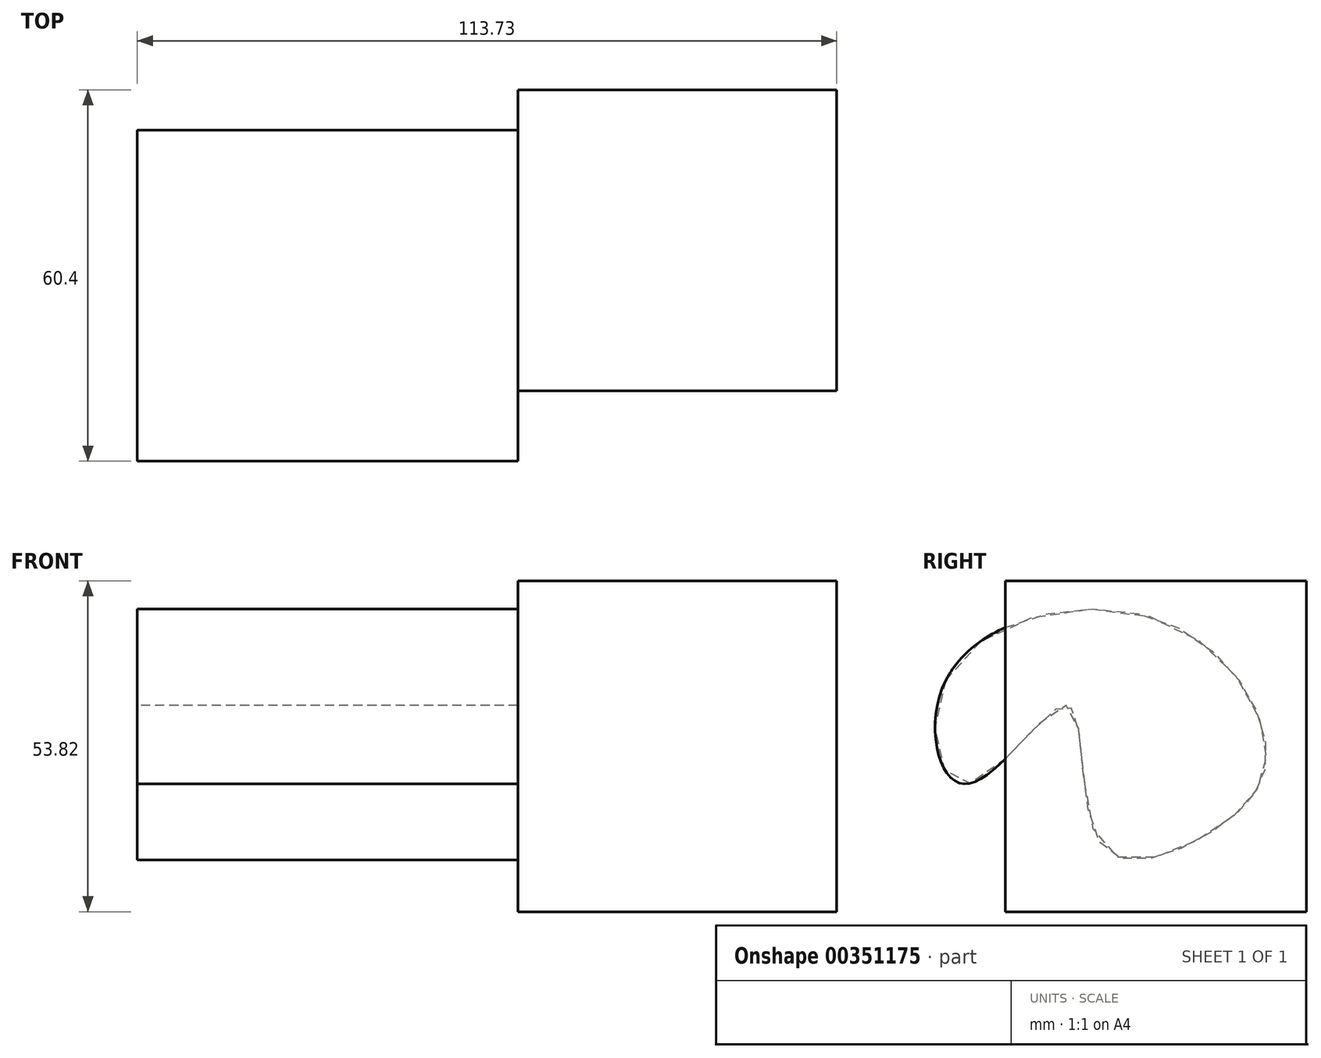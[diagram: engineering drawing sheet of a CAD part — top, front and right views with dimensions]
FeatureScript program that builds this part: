
annotation { "Feature Type Name" : "Feature", "Feature Type Description" : "" }
export const myFeature = defineFeature(function(context is Context, id is Id, definition is map)
    precondition{}
    {
        {
            var Q0;
            Q0=qCreatedBy(makeId("Top.planeOp"),FACE);
            var sketch = newSketch(context, id + "F0", { "sketchPlane" : qUnion([Q0])});
            skLineSegment(sketch, "E0.bottom", {"start": v(-24.41, 23.75) * mm, "end": v(27.4, 23.75) * mm});
            skLineSegment(sketch, "E0.top", {"start": v(-24.41, -25.2) * mm, "end": v(27.4, -25.2) * mm});
            skLineSegment(sketch, "E0.left", {"start": v(-24.41, 23.75) * mm, "end": v(-24.41, -25.2) * mm});
            skLineSegment(sketch, "E0.right", {"start": v(27.4, 23.75) * mm, "end": v(27.4, -25.2) * mm});
            skSolve(sketch);
        }
        {
            var Q0;
            Q0=makeQuery(id+"F0.imprint","IMPRINT",FACE,{"disambiguationData":[TD([[makeQuery(id+"F0.imprint","IMPRINT",EDGE,{"derivedFrom":sQuery(id+"F0.wireOp",EDGE,"E0.bottom")}),-1.0]])]});
            extrude(context, id + "F1", {"entities" : qUnion([Q0]), "depth" : 53.82 * mm});
        }
        {
            var Q0;
            Q0=makeQuery(id+"F1.opExtrude","SWEPT_FACE",FACE,{"disambiguationData":[OSD([sQuery(id+"F0.wireOp",EDGE,"E0.left")])]});
            var sketch = newSketch(context, id + "F2", { "sketchPlane" : qUnion([Q0])});
            skFitSpline(sketch, "E1", {"points": [v(34.9, 37.67) * mm, v(0, 47.45) * mm, v(-17.21, 26.05) * mm, v(-8.64, 13.2) * mm, v(9.6, 10.85) * mm, v(15.15, 33.53) * mm, v(31.5, 20.79) * mm, v(34.9, 37.67) * mm]});
            skSolve(sketch);
        }
        {
            var Q0;
            {var subQ0=sQuery(id+"F2.wireOp",EDGE,"E1");var subQ1=makeQuery(id+"F1.opExtrude","SWEPT_EDGE",EDGE,{"disambiguationData":[OSD([sQuery(id+"F0.wireOp",EDGE,"E0.top"),sQuery(id+"F0.wireOp",EDGE,"E0.left")])]});var subQ2=makeQuery(id+"F2.imprint","INTERSECT",VERTEX,{"disambiguationData":[OD(0.0)],"derivedFrom":[subQ1,subQ0]});Q0=makeQuery(id+"F2.imprint","IMPRINT",FACE,{"disambiguationData":[TD([[makeQuery(id+"F2.imprint","IMPRINT",EDGE,{"disambiguationData":[TD([[subQ2,-1.0]])],"derivedFrom":subQ0}),1.0]])]});}
            var Q1;
            {var subQ0=sQuery(id+"F2.wireOp",EDGE,"E1");var subQ1=makeQuery(id+"F1.opExtrude","SWEPT_EDGE",EDGE,{"disambiguationData":[OSD([sQuery(id+"F0.wireOp",EDGE,"E0.top"),sQuery(id+"F0.wireOp",EDGE,"E0.left")])]});var subQ2=makeQuery(id+"F2.imprint","INTERSECT",VERTEX,{"disambiguationData":[OD(0.0)],"derivedFrom":[subQ1,subQ0]});Q1=makeQuery(id+"F2.imprint","IMPRINT",FACE,{"disambiguationData":[TD([[makeQuery(id+"F2.imprint","IMPRINT",EDGE,{"disambiguationData":[TD([[subQ2,1.0]])],"derivedFrom":subQ0}),1.0]])]});}
            extrude(context, id + "F3", {"entities" : qUnion([Q0, Q1]), "depth" : 12.96 * mm});
        }
        {
            var Q0;
            Q0=makeQuery(id+"F3.opExtrude","CAP_FACE",FACE,{"disambiguationData":[OSD([sQuery(id+"F2.wireOp",EDGE,"E1")])],"isStart":false});
            extrude(context, id + "F4", {"entities" : qUnion([Q0]), "operationType" : NewBodyOperationType.ADD, "depth" : 48.96 * mm});
        }
    });
